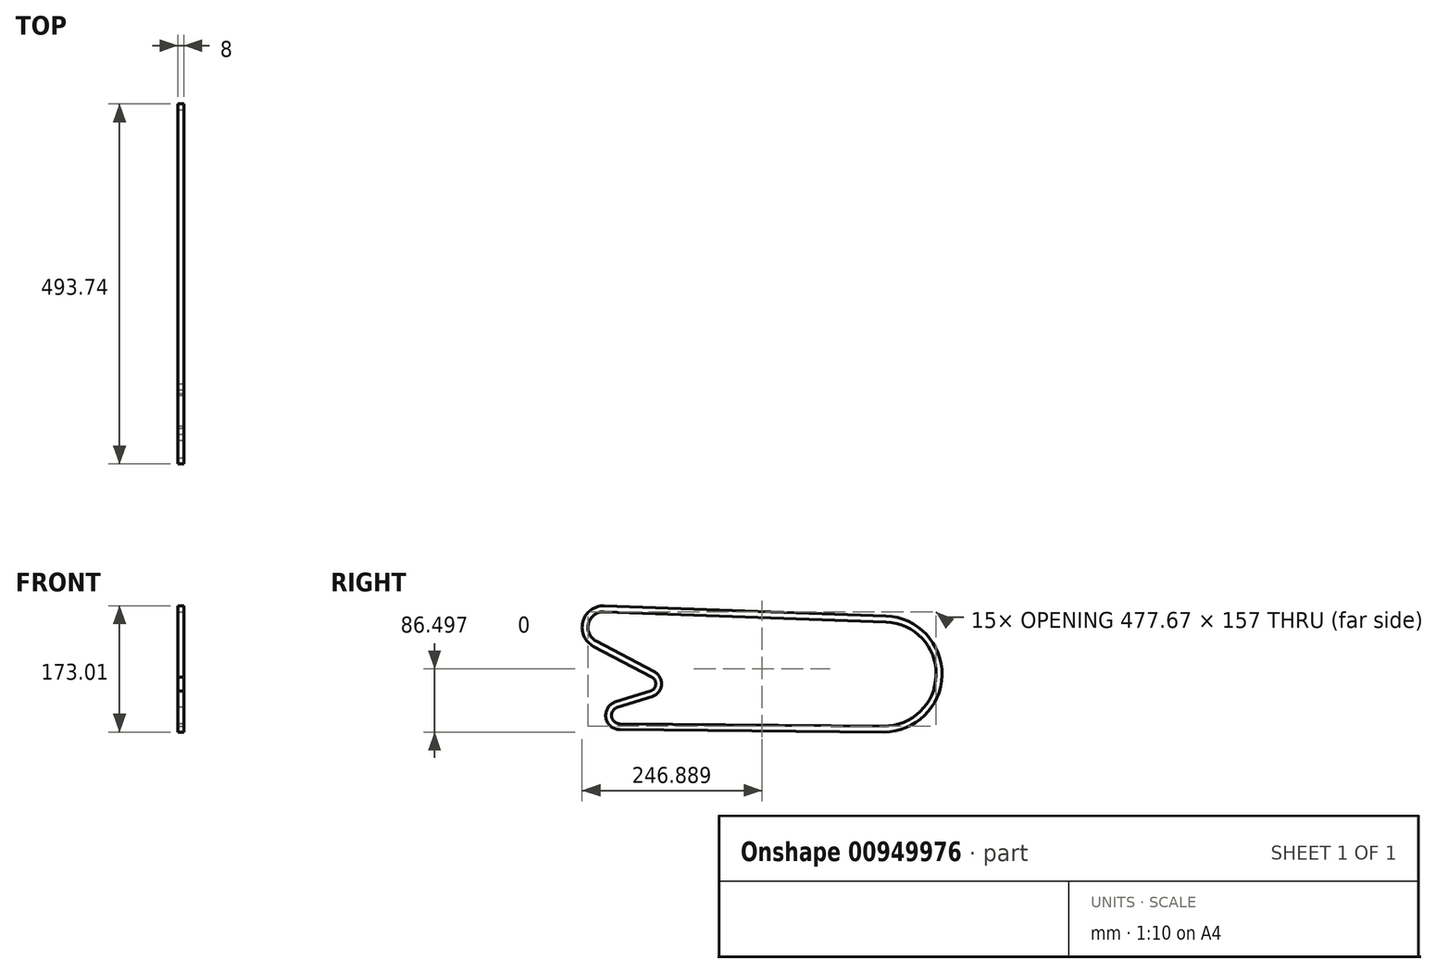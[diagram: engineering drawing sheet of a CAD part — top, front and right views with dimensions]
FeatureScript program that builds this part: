
annotation { "Feature Type Name" : "Feature", "Feature Type Description" : "" }
export const myFeature = defineFeature(function(context is Context, id is Id, definition is map)
    precondition{}
    {
        {
            var Q0;
            Q0=qCreatedBy(makeId("Right.planeOp"),FACE);
            var sketch = newSketch(context, id + "F0", { "sketchPlane" : qUnion([Q0])});
            skArc(sketch, "E0", {"start": v(-0.67, -75) * mm, "mid": v(74.98, -1.7) * mm, "end": v(2.72, 74.95) * mm});
            skArc(sketch, "E1", {"start": v(-383.8, 88.97) * mm, "mid": v(-408.87, 70.42) * mm, "end": v(-396.34, 41.86) * mm});
            skLineSegment(sketch, "E2", {"start": v(-383.8, 88.97) * mm, "end": v(2.72, 74.95) * mm});
            skPoint(sketch, "E3", {"position": v(-383.8, 88.97) * mm});
            skPoint(sketch, "E4", {"position": v(-396.34, 41.86) * mm});
            skPoint(sketch, "E5", {"position": v(-33.33, -67.19) * mm});
            skPoint(sketch, "E6", {"position": v(2.72, 74.95) * mm});
            skArc(sketch, "E7", {"start": v(-319.18, -27.6) * mm, "mid": v(-308.7, -14.64) * mm, "end": v(-316.67, 0) * mm});
            skArc(sketch, "E8", {"start": v(-366.83, -42.47) * mm, "mid": v(-377.2, -58.98) * mm, "end": v(-362.5, -71.79) * mm});
            skLineSegment(sketch, "E9", {"start": v(-396.34, 41.86) * mm, "end": v(-316.67, 0) * mm});
            skLineSegment(sketch, "E10", {"start": v(-362.5, -71.79) * mm, "end": v(-0.67, -75) * mm});
            skLineSegment(sketch, "E11", {"start": v(-366.83, -42.47) * mm, "end": v(-319.18, -27.6) * mm});
            skSolve(sketch);
        }
        {
            var Q0;
            Q0=qCreatedBy(makeId("Front.planeOp"),FACE);
            var sketch = newSketch(context, id + "F1", { "sketchPlane" : qUnion([Q0])});
            skLineSegment(sketch, "E12.bottom", {"start": v(4, 79.56) * mm, "end": v(-4, 79.56) * mm});
            skLineSegment(sketch, "E12.top", {"start": v(4, 71.56) * mm, "end": v(-4, 71.56) * mm});
            skLineSegment(sketch, "E12.left", {"start": v(4, 79.56) * mm, "end": v(4, 71.56) * mm});
            skLineSegment(sketch, "E12.right", {"start": v(-4, 79.56) * mm, "end": v(-4, 71.56) * mm});
            skSolve(sketch);
        }
        {
            var Q0;
            Q0=makeQuery(id+"F1.imprint","IMPRINT",FACE,{"disambiguationData":[TD([[makeQuery(id+"F1.imprint","IMPRINT",EDGE,{"derivedFrom":sQuery(id+"F1.wireOp",EDGE,"E12.bottom")}),1.0]])]});
            var Q1;
            Q1=sQuery(id+"F0.wireOp",EDGE,"E2");
            var Q2;
            Q2=sQuery(id+"F0.wireOp",EDGE,"E0");
            var Q3;
            Q3=sQuery(id+"F0.wireOp",EDGE,"xD74B9uP-QXV6-qiwC-RsyW-5U2eyFzenrgA");
            var Q4;
            Q4=sQuery(id+"F0.wireOp",EDGE,"E1");
            var Q5;
            Q5=sQuery(id+"F0.wireOp",EDGE,"E9");
            var Q6;
            Q6=sQuery(id+"F0.wireOp",EDGE,"E7");
            var Q7;
            Q7=sQuery(id+"F0.wireOp",EDGE,"E11");
            var Q8;
            Q8=sQuery(id+"F0.wireOp",EDGE,"E8");
            var Q9;
            Q9=sQuery(id+"F0.wireOp",EDGE,"E10");
            sweep(context, id + "F2", {"profiles" : qUnion([Q0]), "path" : qUnion([Q1, Q2, Q3, Q4, Q5, Q6, Q7, Q8, Q9])});
        }
    });
